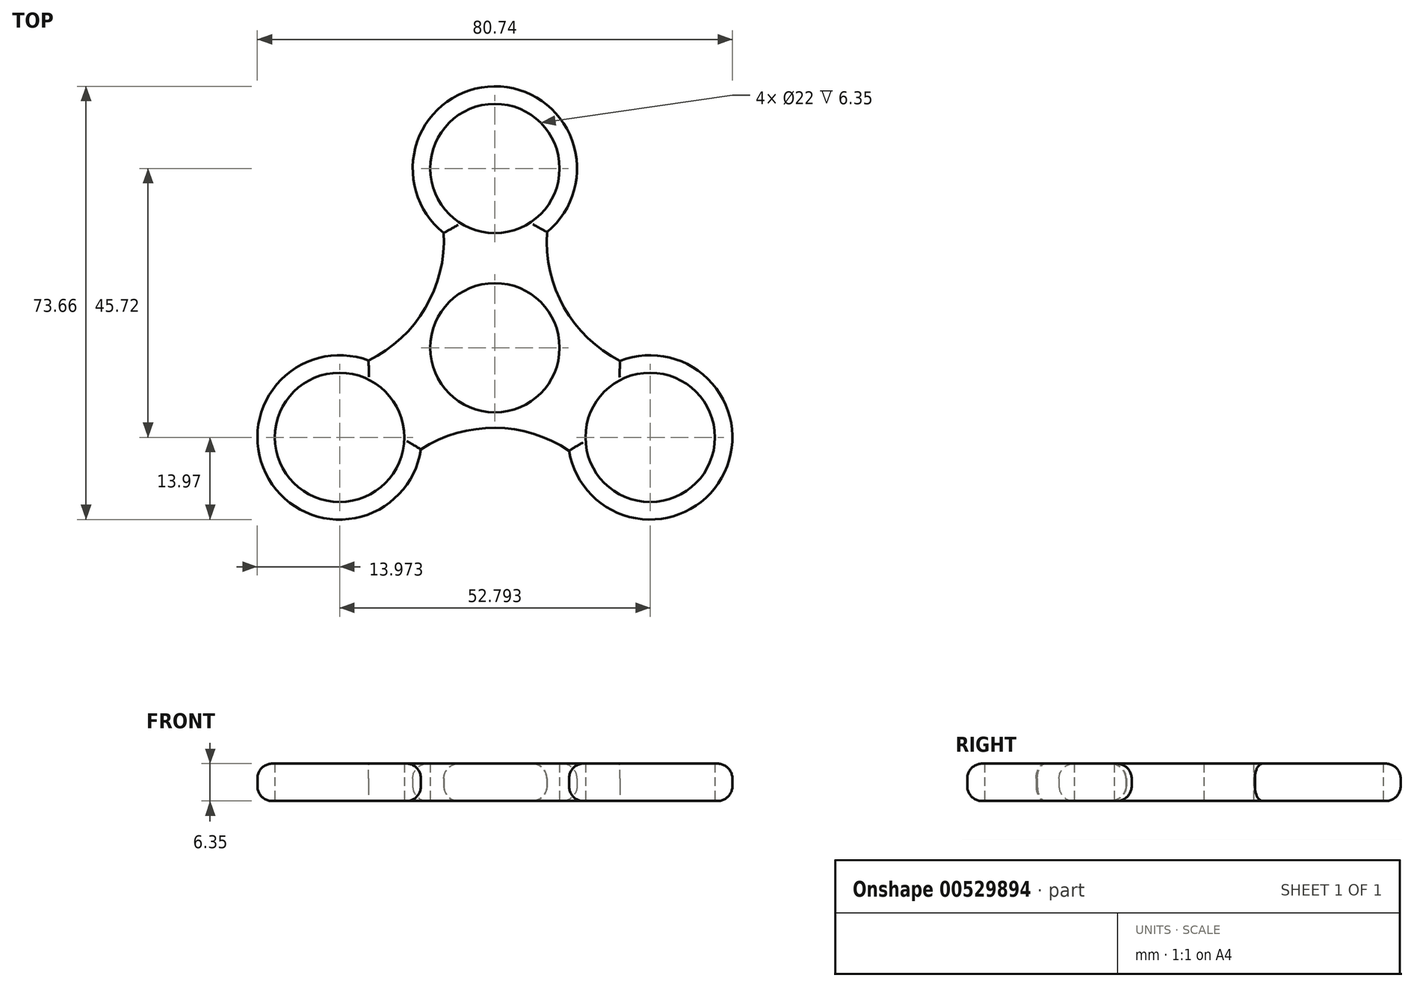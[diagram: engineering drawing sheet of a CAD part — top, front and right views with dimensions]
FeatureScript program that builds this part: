
annotation { "Feature Type Name" : "Feature", "Feature Type Description" : "" }
export const myFeature = defineFeature(function(context is Context, id is Id, definition is map)
    precondition{}
    {
        {
            var Q0;
            Q0=qCreatedBy(makeId("Top.planeOp"),FACE);
            var sketch = newSketch(context, id + "F0", { "sketchPlane" : qUnion([Q0])});
            skCircle(sketch, "E0", {"center": v(0, 0) * mm, "radius": 44.45 * mm});
            skCircle(sketch, "E1", {"center": v(0, 0) * mm, "radius": 11 * mm});
            skLineSegment(sketch, "E2", {"start": v(0, 0) * mm, "end": v(0, 30.48) * mm});
            skCircle(sketch, "E3", {"center": v(0, 30.48) * mm, "radius": 11 * mm});
            skCircle(sketch, "E4", {"center": v(0, 30.48) * mm, "radius": 13.97 * mm});
            skCircle(sketch, "E5.1.0", {"center": v(-26.4, -15.24) * mm, "radius": 13.97 * mm});
            skCircle(sketch, "E5.1.1", {"center": v(-26.4, -15.24) * mm, "radius": 11 * mm});
            skCircle(sketch, "E5.2.0", {"center": v(26.4, -15.24) * mm, "radius": 13.97 * mm});
            skCircle(sketch, "E5.2.1", {"center": v(26.4, -15.24) * mm, "radius": 11 * mm});
            skCircle(sketch, "E6", {"center": v(0, 0) * mm, "radius": 13.97 * mm});
            skArc(sketch, "E7", {"start": v(12.61, -17.51) * mm, "mid": v(0.05, -13.62) * mm, "end": v(-12.58, -17.3) * mm});
            skArc(sketch, "E8.1.0", {"start": v(8.86, 19.68) * mm, "mid": v(11.77, 6.85) * mm, "end": v(21.27, -2.25) * mm});
            skArc(sketch, "E8.2.0", {"start": v(-21.47, -2.17) * mm, "mid": v(-11.82, 6.76) * mm, "end": v(-8.69, 19.54) * mm});
            skSolve(sketch);
        }
        {
            var Q0;
            Q0=makeQuery(id+"F0.imprint","IMPRINT",FACE,{"disambiguationData":[TD([[makeQuery(id+"F0.imprint","IMPRINT",EDGE,{"derivedFrom":sQuery(id+"F0.wireOp",EDGE,"E3")}),-1.0]])]});
            var Q1;
            Q1=makeQuery(id+"F0.imprint","IMPRINT",FACE,{"disambiguationData":[TD([[makeQuery(id+"F0.imprint","IMPRINT",EDGE,{"derivedFrom":sQuery(id+"F0.wireOp",EDGE,"E5.2.0")}),1.0]])]});
            var Q2;
            Q2=makeQuery(id+"F0.imprint","IMPRINT",FACE,{"disambiguationData":[TD([[makeQuery(id+"F0.imprint","IMPRINT",EDGE,{"derivedFrom":sQuery(id+"F0.wireOp",EDGE,"E5.1.0")}),1.0]])]});
            var Q3;
            Q3=makeQuery(id+"F0.imprint","IMPRINT",FACE,{"disambiguationData":[TD([[makeQuery(id+"F0.imprint","IMPRINT",EDGE,{"derivedFrom":sQuery(id+"F0.wireOp",EDGE,"E1")}),-1.0]])]});
            var Q4;
            {var subQ0=sQuery(id+"F0.wireOp",EDGE,"E4");var subQ1=sQuery(id+"F0.wireOp",EDGE,"E2");var subQ2=makeQuery(id+"F0.imprint","INTERSECT",VERTEX,{"derivedFrom":[subQ1,subQ0]});Q4=makeQuery(id+"F0.imprint","IMPRINT",FACE,{"disambiguationData":[TD([[makeQuery(id+"F0.imprint","IMPRINT",EDGE,{"disambiguationData":[TD([[subQ2,1.0]])],"derivedFrom":subQ1}),1.0]])]});}
            var Q5;
            {var subQ0=sQuery(id+"F0.wireOp",EDGE,"E4");var subQ1=sQuery(id+"F0.wireOp",EDGE,"E2");var subQ2=makeQuery(id+"F0.imprint","INTERSECT",VERTEX,{"derivedFrom":[subQ1,subQ0]});Q5=makeQuery(id+"F0.imprint","IMPRINT",FACE,{"disambiguationData":[TD([[makeQuery(id+"F0.imprint","IMPRINT",EDGE,{"disambiguationData":[TD([[subQ2,1.0]])],"derivedFrom":subQ1}),-1.0]])]});}
            var Q6;
            {var subQ0=sQuery(id+"F0.wireOp",EDGE,"E7");var subQ1=sQuery(id+"F0.wireOp",EDGE,"E5.2.0");var subQ2=makeQuery(id+"F0.imprint","INTERSECT",VERTEX,{"derivedFrom":[subQ1,subQ0]});Q6=makeQuery(id+"F0.imprint","IMPRINT",FACE,{"disambiguationData":[TD([[makeQuery(id+"F0.imprint","IMPRINT",EDGE,{"disambiguationData":[TD([[subQ2,1.0]])],"derivedFrom":subQ1}),-1.0]])]});}
            var Q7;
            {var subQ0=sQuery(id+"F0.wireOp",EDGE,"E7");var subQ1=sQuery(id+"F0.wireOp",EDGE,"E5.1.0");var subQ2=makeQuery(id+"F0.imprint","INTERSECT",VERTEX,{"derivedFrom":[subQ1,subQ0]});Q7=makeQuery(id+"F0.imprint","IMPRINT",FACE,{"disambiguationData":[TD([[makeQuery(id+"F0.imprint","IMPRINT",EDGE,{"disambiguationData":[TD([[subQ2,-1.0]])],"derivedFrom":subQ1}),-1.0]])]});}
            extrude(context, id + "F1", {"entities" : qUnion([Q0, Q1, Q2, Q3, Q4, Q5, Q6, Q7]), "depth" : 6.35 * mm, "offsetDistance" : 25.4 * mm});
        }
        {
            var Q0;
            Q0=makeQuery(id+"F1.opExtrude","CAP_EDGE",EDGE,{"disambiguationData":[OSD([sQuery(id+"F0.wireOp",EDGE,"E8.1.0")])],"isStart":false});
            var Q1;
            Q1=makeQuery(id+"F1.opExtrude","CAP_EDGE",EDGE,{"disambiguationData":[OSD([sQuery(id+"F0.wireOp",EDGE,"E8.2.0")])],"isStart":false});
            var Q2;
            Q2=makeQuery(id+"F1.opExtrude","CAP_EDGE",EDGE,{"disambiguationData":[OSD([sQuery(id+"F0.wireOp",EDGE,"E7")])],"isStart":false});
            var Q3;
            Q3=makeQuery(id+"F1.opExtrude","CAP_EDGE",EDGE,{"disambiguationData":[OSD([sQuery(id+"F0.wireOp",EDGE,"E5.1.0")])],"isStart":false});
            var Q4;
            Q4=makeQuery(id+"F1.opExtrude","CAP_EDGE",EDGE,{"disambiguationData":[OSD([sQuery(id+"F0.wireOp",EDGE,"E5.2.0")])],"isStart":false});
            var Q5;
            Q5=makeQuery(id+"F1.opExtrude","CAP_EDGE",EDGE,{"disambiguationData":[OSD([sQuery(id+"F0.wireOp",EDGE,"E4")])],"isStart":false});
            var Q6;
            Q6=makeQuery(id+"F1.opExtrude","CAP_EDGE",EDGE,{"disambiguationData":[OSD([sQuery(id+"F0.wireOp",EDGE,"E8.2.0")])],"isStart":true});
            var Q7;
            Q7=makeQuery(id+"F1.opExtrude","CAP_EDGE",EDGE,{"disambiguationData":[OSD([sQuery(id+"F0.wireOp",EDGE,"E8.1.0")])],"isStart":true});
            var Q8;
            Q8=makeQuery(id+"F1.opExtrude","CAP_EDGE",EDGE,{"disambiguationData":[OSD([sQuery(id+"F0.wireOp",EDGE,"E4")])],"isStart":true});
            var Q9;
            Q9=makeQuery(id+"F1.opExtrude","CAP_EDGE",EDGE,{"disambiguationData":[OSD([sQuery(id+"F0.wireOp",EDGE,"E5.2.0")])],"isStart":true});
            var Q10;
            Q10=makeQuery(id+"F1.opExtrude","CAP_EDGE",EDGE,{"disambiguationData":[OSD([sQuery(id+"F0.wireOp",EDGE,"E5.1.0")])],"isStart":true});
            var Q11;
            Q11=makeQuery(id+"F1.opExtrude","CAP_EDGE",EDGE,{"disambiguationData":[OSD([sQuery(id+"F0.wireOp",EDGE,"E7")])],"isStart":true});
            fillet(context, id + "F2", {"entities" : qUnion([Q0, Q1, Q2, Q3, Q4, Q5, Q6, Q7, Q8, Q9, Q10, Q11]), "radius" : 2.54 * mm, "tangentPropagation" : true, "allowEdgeOverflow" : false});
        }
    });
